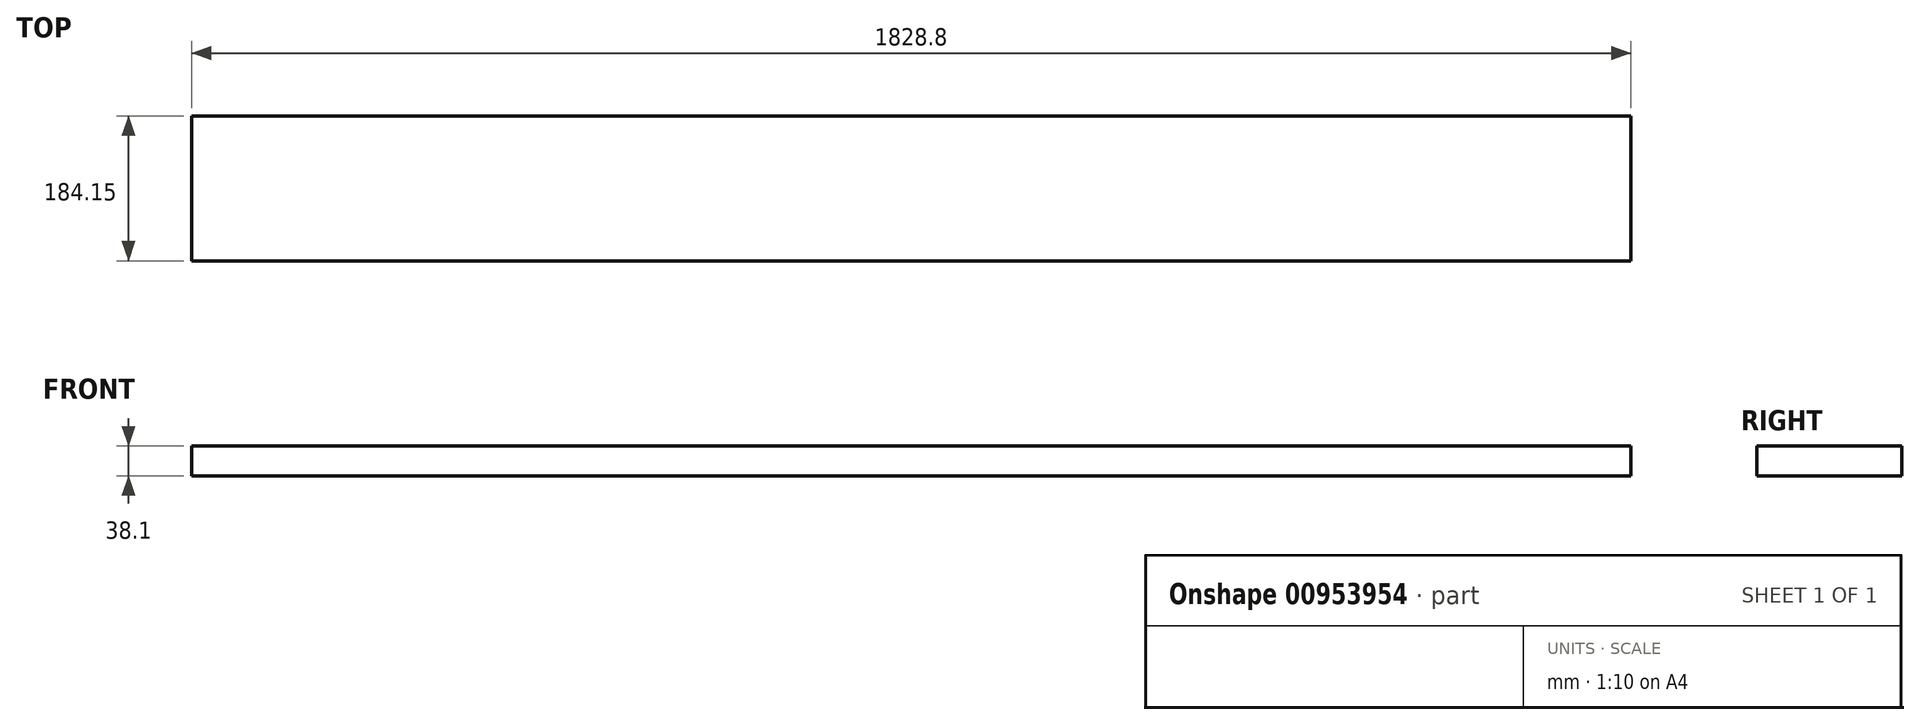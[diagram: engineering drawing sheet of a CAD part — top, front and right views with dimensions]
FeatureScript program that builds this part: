
annotation { "Feature Type Name" : "Feature", "Feature Type Description" : "" }
export const myFeature = defineFeature(function(context is Context, id is Id, definition is map)
    precondition{}
    {
        {
            var Q0;
            Q0=qCreatedBy(makeId("Top.planeOp"),FACE);
            var sketch = newSketch(context, id + "F0", { "sketchPlane" : qUnion([Q0])});
            skLineSegment(sketch, "E0.bottom", {"start": v(0, 0) * mm, "end": v(1828.8, 0) * mm});
            skLineSegment(sketch, "E0.top", {"start": v(0, 184.15) * mm, "end": v(1828.8, 184.15) * mm});
            skLineSegment(sketch, "E0.left", {"start": v(0, 0) * mm, "end": v(0, 184.15) * mm});
            skLineSegment(sketch, "E0.right", {"start": v(1828.8, 0) * mm, "end": v(1828.8, 184.15) * mm});
            skSolve(sketch);
        }
        {
            var Q0;
            Q0 = qSketchRegion(id + "F0", true);
            extrude(context, id + "F1", {"entities" : qUnion([Q0]), "depth" : 38.1 * mm, "offsetDistance" : 25.4 * mm});
        }
    });
